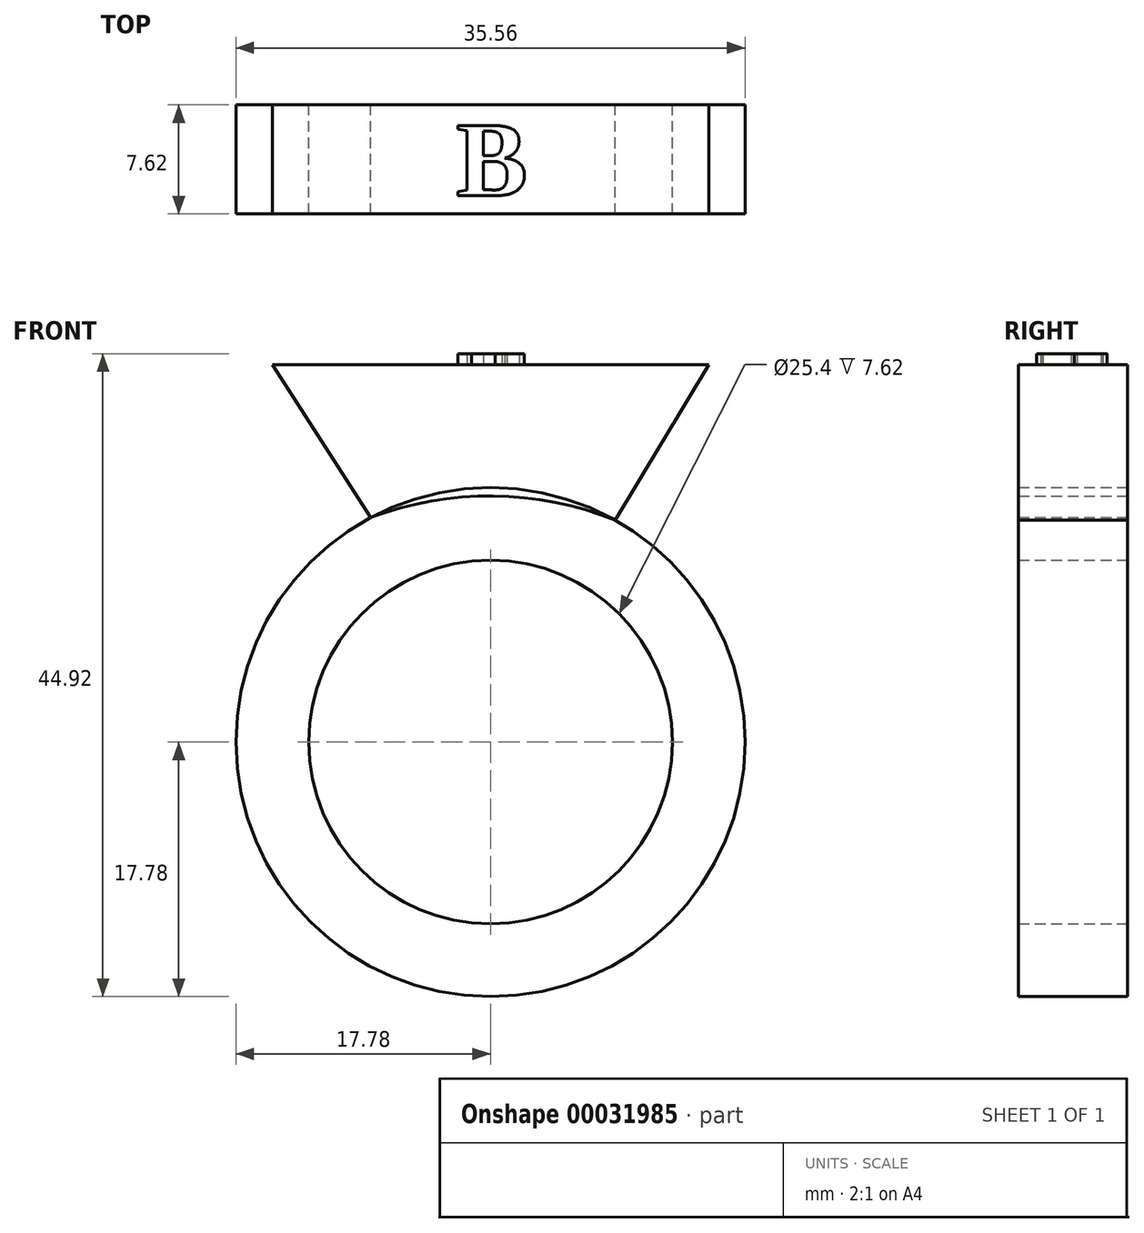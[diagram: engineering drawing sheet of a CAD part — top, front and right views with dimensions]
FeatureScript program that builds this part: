
annotation { "Feature Type Name" : "Feature", "Feature Type Description" : "" }
export const myFeature = defineFeature(function(context is Context, id is Id, definition is map)
    precondition{}
    {
        {
            var Q0;
            Q0=qCreatedBy(makeId("Front.planeOp"),FACE);
            var sketch = newSketch(context, id + "F0", { "sketchPlane" : qUnion([Q0])});
            skCircle(sketch, "E0", {"center": v(0, 0) * mm, "radius": 17.78 * mm});
            skCircle(sketch, "E1", {"center": v(0, 0) * mm, "radius": 12.7 * mm});
            skSolve(sketch);
        }
        {
            var Q0;
            Q0=makeQuery(id+"F0.imprint","IMPRINT",FACE,{"disambiguationData":[TD([[makeQuery(id+"F0.imprint","IMPRINT",EDGE,{"derivedFrom":sQuery(id+"F0.wireOp",EDGE,"E0")}),1.0]])]});
            extrude(context, id + "F1", {"entities" : qUnion([Q0]), "depth" : 7.62 * mm});
        }
        {
            var Q0;
            Q0=makeQuery(id+"F1.opExtrude","CAP_FACE",FACE,{"disambiguationData":[OSD([sQuery(id+"F0.wireOp",EDGE,"E0"),sQuery(id+"F0.wireOp",EDGE,"E1")])],"isStart":true});
            var sketch = newSketch(context, id + "F2", { "sketchPlane" : qUnion([Q0])});
            skLineSegment(sketch, "E2", {"start": v(-8.7, 15.5) * mm, "end": v(-15.26, 26.38) * mm});
            skLineSegment(sketch, "E3", {"start": v(-15.26, 26.38) * mm, "end": v(15.22, 26.38) * mm});
            skLineSegment(sketch, "E4", {"start": v(15.22, 26.38) * mm, "end": v(8.36, 15.7) * mm});
            skArc(sketch, "E5", {"start": v(8.36, 15.7) * mm, "mid": v(-0.19, 17.2) * mm, "end": v(-8.7, 15.5) * mm});
            skSolve(sketch);
        }
        {
            var Q0;
            Q0 = qSketchRegion(id + "F2", true);
            var Q1;
            {var subQ2=sQuery(id+"F2.wireOp",EDGE,"E2");Q1=makeQuery(id+"F2.imprint","IMPRINT",FACE,{"disambiguationData":[TD([[makeQuery(id+"F2.imprint","IMPRINT",EDGE,{"derivedFrom":subQ2}),-1.0]])]});}
            extrude(context, id + "F3", {"entities" : qUnion([Q0, Q1]), "oppositeDirection" : true, "depth" : 7.62 * mm});
        }
        {
            var Q0;
            Q0=makeQuery(id+"F3.opExtrude","SWEPT_FACE",FACE,{"disambiguationData":[OSD([sQuery(id+"F2.wireOp",EDGE,"E3")])]});
            var sketch = newSketch(context, id + "F4", { "sketchPlane" : qUnion([Q0])});
            skText(sketch, "E6", { "text": "B", "fontName": "Tinos-Bold.ttf"});
            const initialGuessF4  = {"E6": [-0.0024, -0.00632, 1, 0, 0.00537]};
            skSetInitialGuess(sketch, initialGuessF4);
            skSolve(sketch);
        }
        {
            var Q0;
            Q0 = qSketchRegion(id + "F4", true);
            extrude(context, id + "F5", {"entities" : qUnion([Q0]), "operationType" : NewBodyOperationType.ADD, "depth" : 0.76 * mm});
        }
    });
